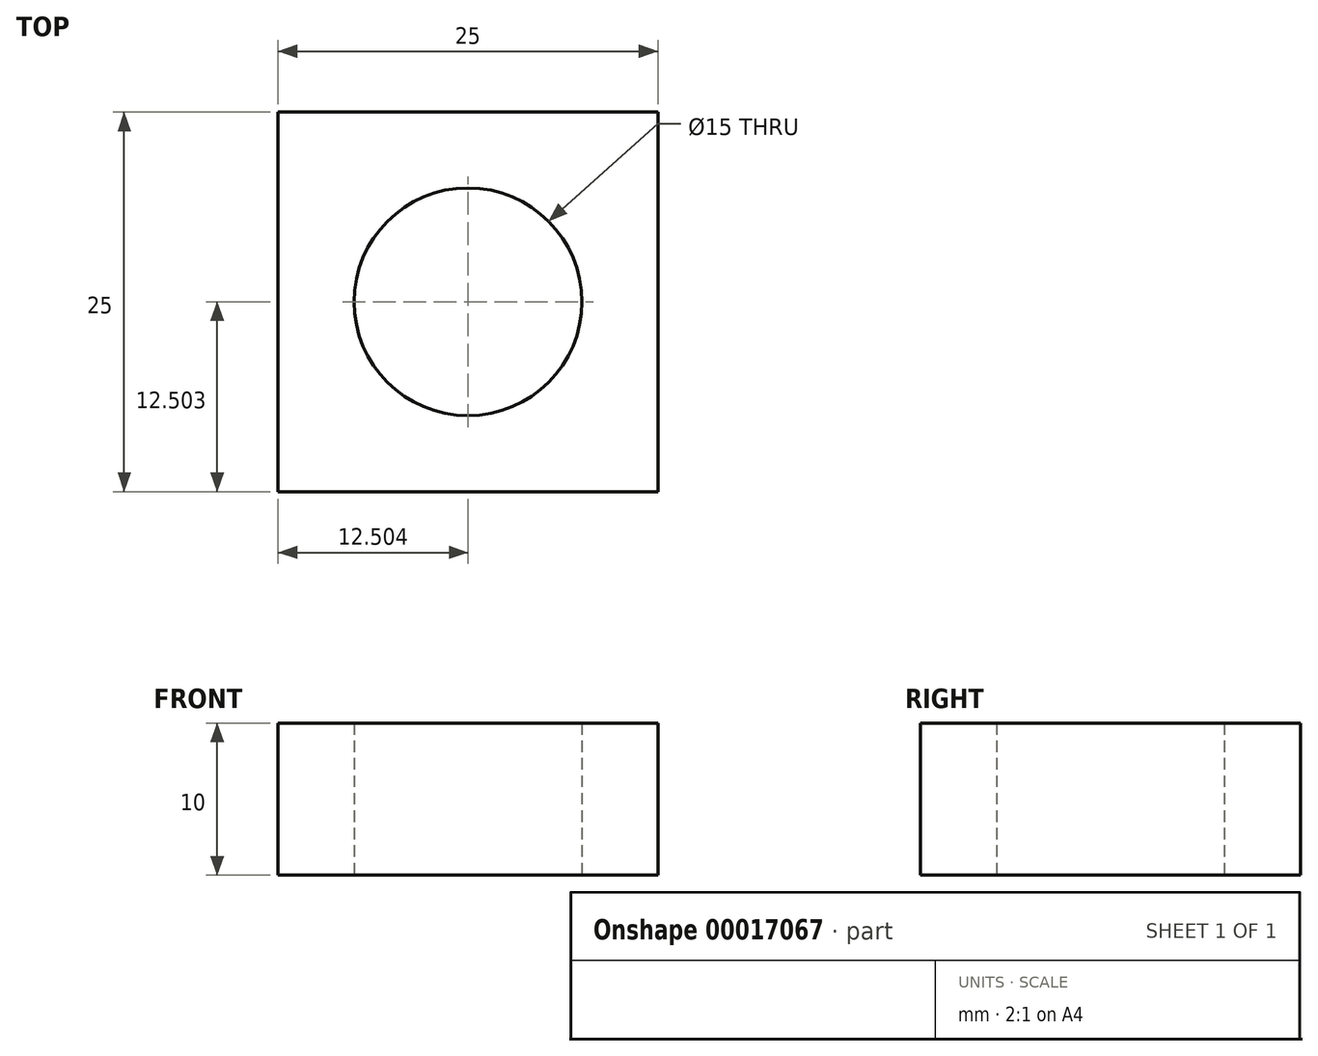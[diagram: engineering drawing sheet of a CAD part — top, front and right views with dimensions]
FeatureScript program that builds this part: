
annotation { "Feature Type Name" : "Feature", "Feature Type Description" : "" }
export const myFeature = defineFeature(function(context is Context, id is Id, definition is map)
    precondition{}
    {
        {
            var Q0;
            Q0=qCreatedBy(makeId("Top.planeOp"),FACE);
            var sketch = newSketch(context, id + "F0", { "sketchPlane" : qUnion([Q0])});
            skLineSegment(sketch, "E0.bottom", {"start": v(-15.57, -2) * mm, "end": v(9.43, -2) * mm});
            skLineSegment(sketch, "E0.top", {"start": v(-15.57, -27) * mm, "end": v(9.43, -27) * mm});
            skLineSegment(sketch, "E0.left", {"start": v(-15.57, -2) * mm, "end": v(-15.57, -27) * mm});
            skLineSegment(sketch, "E0.right", {"start": v(9.43, -2) * mm, "end": v(9.43, -27) * mm});
            skCircle(sketch, "E1", {"center": v(-3.07, -14.5) * mm, "radius": 7.5 * mm});
            skSolve(sketch);
        }
        {
            var Q0;
            Q0 = qSketchRegion(id + "F0", true);
            extrude(context, id + "F1", {"entities" : qUnion([Q0]), "depth" : 10 * mm});
        }
    });
